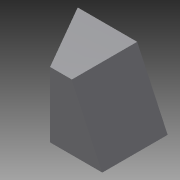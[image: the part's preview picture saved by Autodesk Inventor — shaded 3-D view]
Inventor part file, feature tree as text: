
AUTODESK INVENTOR PART (.ipt)
format: ipt  version: 2011 SP1 (Build 150282100, 282)  size: 76,288 bytes
history: native  units: mm
features: extrude x2, sketch x2
ambient origin geometry x8: Origin, YZ Plane, XZ Plane, XY Plane, X Axis, Y Axis, Z Axis, Center Point
bodies: Solid1 (feature_tree)
feature tree (4):
  extrude  "Extrusion1"  Depth=15.0mm
  extrude  "Extrusion2"  Depth=15.0mm TaperAngle=0.0deg
  sketch  "Sketch1"  dims[d0=15.0mm d1=15.0mm]
  sketch  "Sketch2"  dims[d3=120.0deg d4=15.0mm d5=0.0mm d6=5.0mm d7=11.34464mm d8=15.0mm d9=0.0mm]
